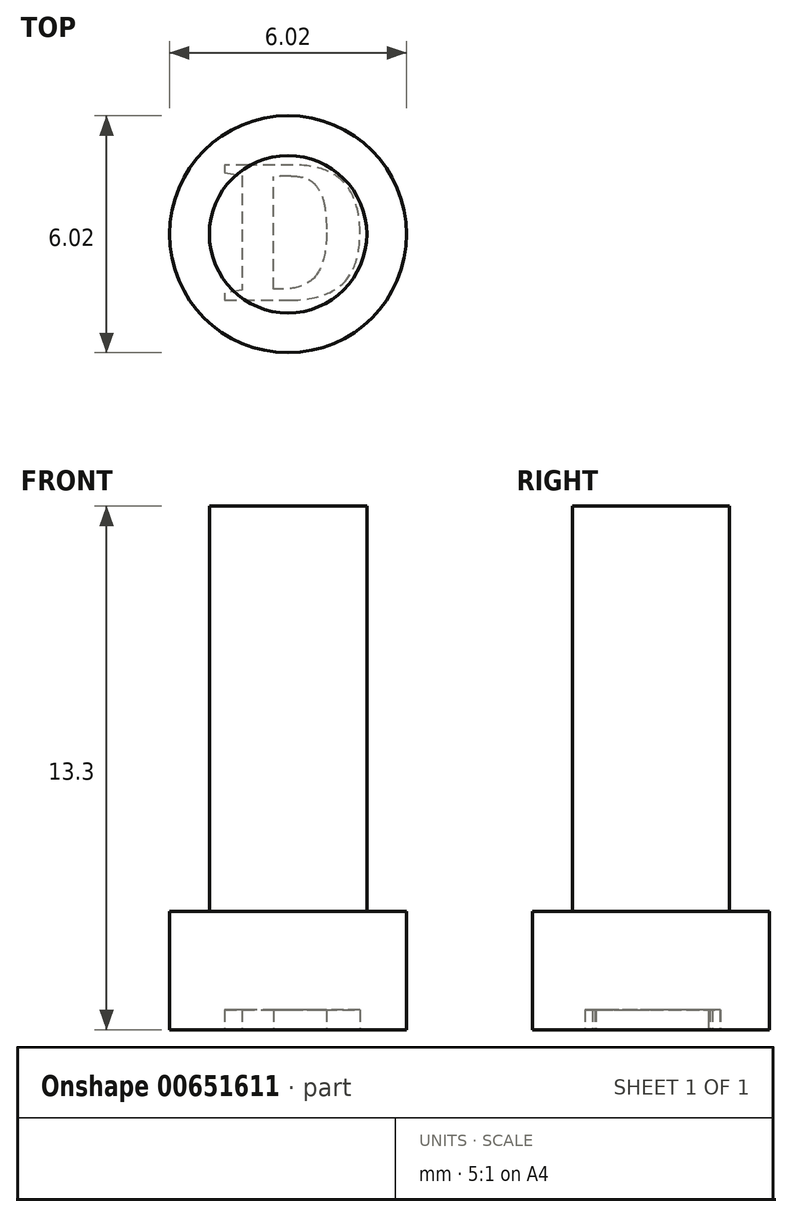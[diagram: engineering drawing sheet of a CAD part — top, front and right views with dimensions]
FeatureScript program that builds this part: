
annotation { "Feature Type Name" : "Feature", "Feature Type Description" : "" }
export const myFeature = defineFeature(function(context is Context, id is Id, definition is map)
    precondition{}
    {
        {
            var Q0;
            Q0=qCreatedBy(makeId("Top.planeOp"),FACE);
            var sketch = newSketch(context, id + "F0", { "sketchPlane" : qUnion([Q0])});
            skCircle(sketch, "E0", {"center": v(0, 0) * mm, "radius": 2 * mm});
            skSolve(sketch);
        }
        {
            var Q0;
            Q0=makeQuery(id+"F0.imprint","IMPRINT",FACE,{"disambiguationData":[TD([[makeQuery(id+"F0.imprint","IMPRINT",EDGE,{"derivedFrom":sQuery(id+"F0.wireOp",EDGE,"E0")}),1.0]])]});
            extrude(context, id + "F1", {"entities" : qUnion([Q0]), "depth" : 10.3 * mm});
        }
        {
            var Q0;
            Q0=makeQuery(id+"F1.opExtrude","CAP_FACE",FACE,{"disambiguationData":[OSD([sQuery(id+"F0.wireOp",EDGE,"E0")])],"isStart":true});
            var sketch = newSketch(context, id + "F2", { "sketchPlane" : qUnion([Q0])});
            skCircle(sketch, "E1", {"center": v(0, 0) * mm, "radius": 3.01 * mm});
            skSolve(sketch);
        }
        {
            var Q0;
            Q0=makeQuery(id+"F2.imprint","IMPRINT",FACE,{"disambiguationData":[TD([[makeQuery(id+"F2.imprint","IMPRINT",EDGE,{"derivedFrom":makeQuery(id+"F1.opExtrude","CAP_EDGE",EDGE,{"disambiguationData":[OSD([sQuery(id+"F0.wireOp",EDGE,"E0")])],"isStart":true})}),-1.0]])]});
            var Q1;
            Q1=makeQuery(id+"F2.imprint","IMPRINT",FACE,{"disambiguationData":[TD([[makeQuery(id+"F2.imprint","IMPRINT",EDGE,{"derivedFrom":sQuery(id+"F2.wireOp",EDGE,"E1")}),1.0]])]});
            extrude(context, id + "F3", {"entities" : qUnion([Q0, Q1]), "operationType" : NewBodyOperationType.ADD, "depth" : 3 * mm});
        }
        {
            var Q0;
            Q0=makeQuery(id+"F3.opExtrude","CAP_FACE",FACE,{"disambiguationData":[OSD([sQuery(id+"F2.wireOp",EDGE,"E1")])],"isStart":false});
            var sketch = newSketch(context, id + "F4", { "sketchPlane" : qUnion([Q0])});
            skText(sketch, "E2", { "text": "D", "fontName": "Tinos-Bold.ttf"});
            const initialGuessF4  = {"E2": [-0.0017, -0.00175, 1, 0, 0.00377]};
            skSetInitialGuess(sketch, initialGuessF4);
            skSolve(sketch);
        }
        {
            var Q0;
            Q0=makeQuery(id+"F4.imprint","IMPRINT",FACE,{"disambiguationData":[TD([[makeQuery(id+"F4.imprint","IMPRINT",EDGE,{"derivedFrom":sQuery(id+"F4.wireOp",EDGE,"E2.sketch_text.stroke-0")}),-1.0]])]});
            extrude(context, id + "F5", {"entities" : qUnion([Q0]), "operationType" : NewBodyOperationType.REMOVE, "oppositeDirection" : true, "depth" : 0.5 * mm});
        }
    });
